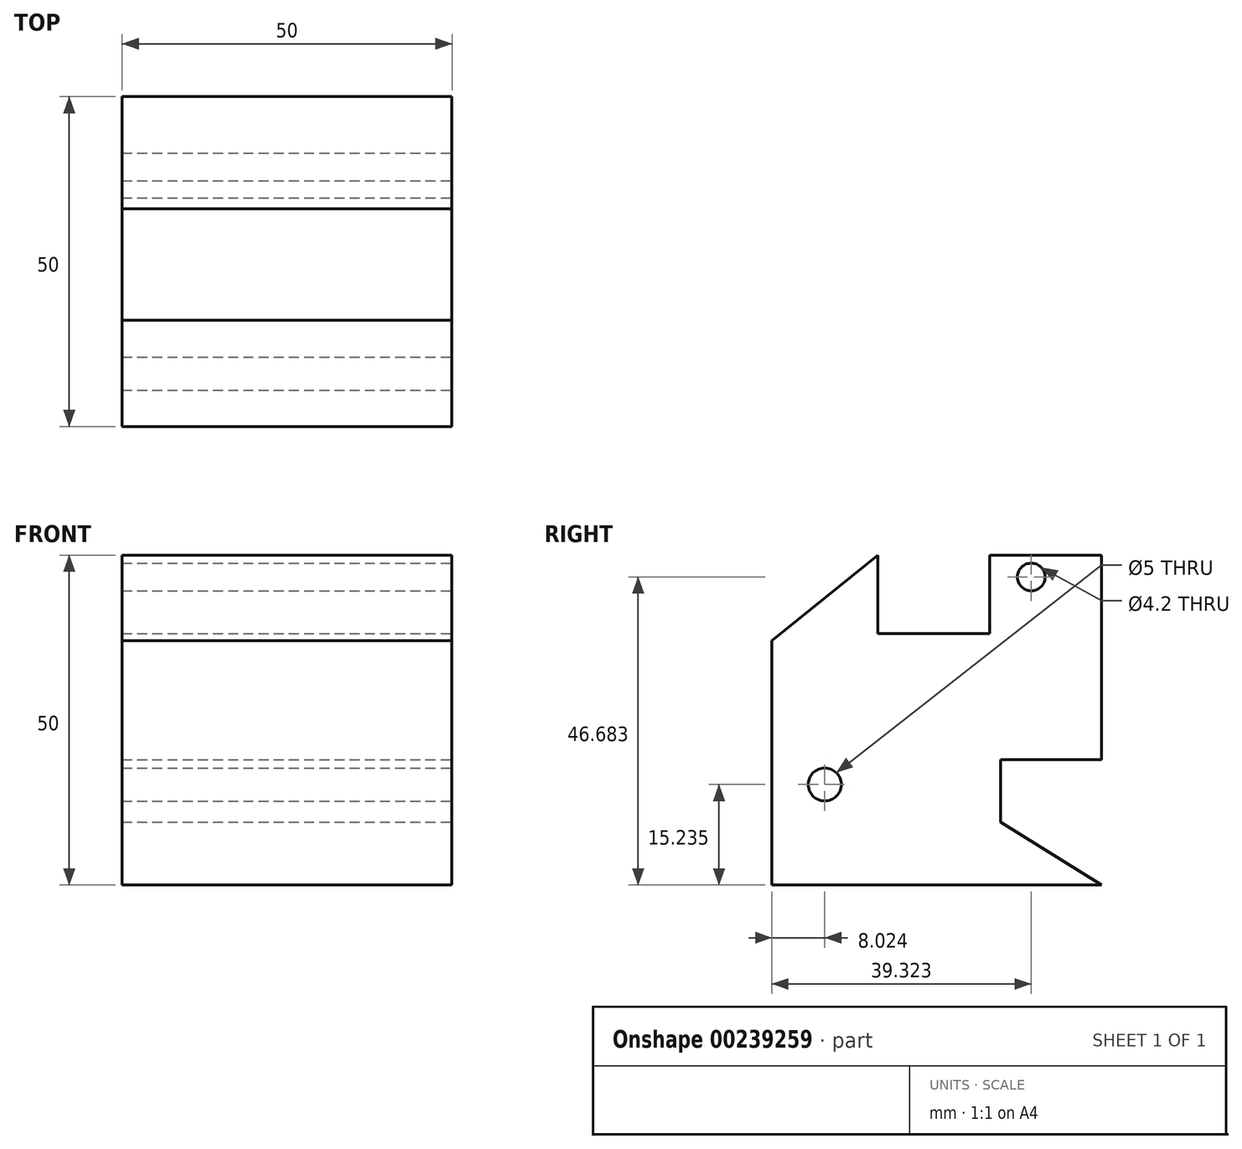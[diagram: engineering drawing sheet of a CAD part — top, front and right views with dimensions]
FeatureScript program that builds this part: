
annotation { "Feature Type Name" : "Feature", "Feature Type Description" : "" }
export const myFeature = defineFeature(function(context is Context, id is Id, definition is map)
    precondition{}
    {
        {
            var Q0;
            Q0=qCreatedBy(makeId("Top.planeOp"),FACE);
            var sketch = newSketch(context, id + "F0", { "sketchPlane" : qUnion([Q0])});
            skLineSegment(sketch, "E0.bottom", {"start": v(-45.02, 15.34) * mm, "end": v(4.98, 15.34) * mm});
            skLineSegment(sketch, "E0.top", {"start": v(-45.02, -34.66) * mm, "end": v(4.98, -34.66) * mm});
            skLineSegment(sketch, "E0.left", {"start": v(-45.02, 15.34) * mm, "end": v(-45.02, -34.66) * mm});
            skLineSegment(sketch, "E0.right", {"start": v(4.98, 15.34) * mm, "end": v(4.98, -34.66) * mm});
            skSolve(sketch);
        }
        {
            var Q0;
            Q0 = qSketchRegion(id + "F0", true);
            extrude(context, id + "F1", {"entities" : qUnion([Q0]), "depth" : 50 * mm});
        }
        {
            var Q0;
            Q0=makeQuery(id+"F1.opExtrude","SWEPT_FACE",FACE,{"disambiguationData":[OSD([sQuery(id+"F0.wireOp",EDGE,"E0.right")])]});
            var sketch = newSketch(context, id + "F2", { "sketchPlane" : qUnion([Q0])});
            skLineSegment(sketch, "E1", {"start": v(-18.56, 50) * mm, "end": v(-34.66, 37.03) * mm});
            skSolve(sketch);
        }
        {
            var Q0;
            Q0 = qSketchRegion(id + "F2", true);
            var Q1;
            {var subQ0=sQuery(id+"F2.wireOp",EDGE,"E1");Q1=makeQuery(id+"F2.imprint","IMPRINT",FACE,{"disambiguationData":[TD([[makeQuery(id+"F2.imprint","IMPRINT",EDGE,{"derivedFrom":subQ0}),-1.0]])]});}
            extrude(context, id + "F3", {"entities" : qUnion([Q0, Q1]), "operationType" : NewBodyOperationType.REMOVE, "oppositeDirection" : true, "depth" : 50 * mm});
        }
        {
            var Q0;
            Q0=makeQuery(id+"F1.opExtrude","SWEPT_FACE",FACE,{"disambiguationData":[OSD([sQuery(id+"F0.wireOp",EDGE,"E0.right")])]});
            var sketch = newSketch(context, id + "F4", { "sketchPlane" : qUnion([Q0])});
            skCircle(sketch, "E2", {"center": v(-26.64, 15.24) * mm, "radius": 2.5 * mm});
            skSolve(sketch);
        }
        {
            var Q0;
            Q0=makeQuery(id+"F4.imprint","IMPRINT",FACE,{"disambiguationData":[TD([[makeQuery(id+"F4.imprint","IMPRINT",EDGE,{"derivedFrom":sQuery(id+"F4.wireOp",EDGE,"E2")}),1.0]])]});
            extrude(context, id + "F5", {"entities" : qUnion([Q0]), "operationType" : NewBodyOperationType.ADD, "endBound" : BoundingType.THROUGH_ALL, "depth" : 25.4 * mm});
        }
        {
            var Q0;
            Q0=makeQuery(id+"F5.opExtrude","CAP_FACE",FACE,{"disambiguationData":[OSD([sQuery(id+"F4.wireOp",EDGE,"E2")])],"isStart":false});
            extrude(context, id + "F6", {"entities" : qUnion([Q0]), "operationType" : NewBodyOperationType.REMOVE, "endBound" : BoundingType.THROUGH_ALL, "oppositeDirection" : true, "depth" : 25.4 * mm});
        }
        {
            var Q0;
            Q0=makeQuery(id+"F1.opExtrude","SWEPT_FACE",FACE,{"disambiguationData":[OSD([sQuery(id+"F0.wireOp",EDGE,"E0.right")])]});
            var sketch = newSketch(context, id + "F7", { "sketchPlane" : qUnion([Q0])});
            skCircle(sketch, "E3", {"center": v(4.66, 46.68) * mm, "radius": 2.1 * mm});
            skSolve(sketch);
        }
        {
            var Q0;
            Q0=makeQuery(id+"F7.imprint","IMPRINT",FACE,{"disambiguationData":[TD([[makeQuery(id+"F7.imprint","IMPRINT",EDGE,{"derivedFrom":sQuery(id+"F7.wireOp",EDGE,"E3")}),1.0]])]});
            extrude(context, id + "F8", {"entities" : qUnion([Q0]), "operationType" : NewBodyOperationType.REMOVE, "endBound" : BoundingType.THROUGH_ALL, "oppositeDirection" : true, "depth" : 25.4 * mm});
        }
        {
            var Q0;
            Q0=makeQuery(id+"F1.opExtrude","SWEPT_FACE",FACE,{"disambiguationData":[OSD([sQuery(id+"F0.wireOp",EDGE,"E0.right")])]});
            var sketch = newSketch(context, id + "F9", { "sketchPlane" : qUnion([Q0])});
            skLineSegment(sketch, "E4.bottom", {"start": v(-18.56, 50) * mm, "end": v(-1.67, 50) * mm});
            skLineSegment(sketch, "E4.top", {"start": v(-18.56, 38.12) * mm, "end": v(-1.67, 38.12) * mm});
            skLineSegment(sketch, "E4.left", {"start": v(-18.56, 50) * mm, "end": v(-18.56, 38.12) * mm});
            skLineSegment(sketch, "E4.right", {"start": v(-1.67, 50) * mm, "end": v(-1.67, 38.12) * mm});
            skSolve(sketch);
        }
        {
            var Q0;
            Q0=makeQuery(id+"F9.imprint","IMPRINT",FACE,{"disambiguationData":[TD([[makeQuery(id+"F9.imprint","IMPRINT",EDGE,{"derivedFrom":sQuery(id+"F9.wireOp",EDGE,"E4.bottom")}),1.0]])]});
            extrude(context, id + "F10", {"entities" : qUnion([Q0]), "operationType" : NewBodyOperationType.REMOVE, "endBound" : BoundingType.THROUGH_ALL, "oppositeDirection" : true, "depth" : 25 * mm});
        }
        {
            var Q0;
            Q0=makeQuery(id+"F1.opExtrude","SWEPT_FACE",FACE,{"disambiguationData":[OSD([sQuery(id+"F0.wireOp",EDGE,"E0.right")])]});
            var sketch = newSketch(context, id + "F11", { "sketchPlane" : qUnion([Q0])});
            skLineSegment(sketch, "E5", {"start": v(15.34, 19.02) * mm, "end": v(0, 19.02) * mm});
            skLineSegment(sketch, "E6", {"start": v(0, 19.02) * mm, "end": v(0, 9.55) * mm});
            skLineSegment(sketch, "E7", {"start": v(0, 9.55) * mm, "end": v(15.34, 0) * mm});
            skLineSegment(sketch, "E8", {"start": v(15.34, 0) * mm, "end": v(15.34, 19.02) * mm});
            skSolve(sketch);
        }
        {
            var Q0;
            Q0=makeQuery(id+"F11.imprint","IMPRINT",FACE,{"disambiguationData":[TD([[makeQuery(id+"F11.imprint","IMPRINT",EDGE,{"derivedFrom":sQuery(id+"F11.wireOp",EDGE,"E5")}),1.0]])]});
            extrude(context, id + "F12", {"entities" : qUnion([Q0]), "operationType" : NewBodyOperationType.REMOVE, "endBound" : BoundingType.THROUGH_ALL, "oppositeDirection" : true, "depth" : 25 * mm});
        }
    });
